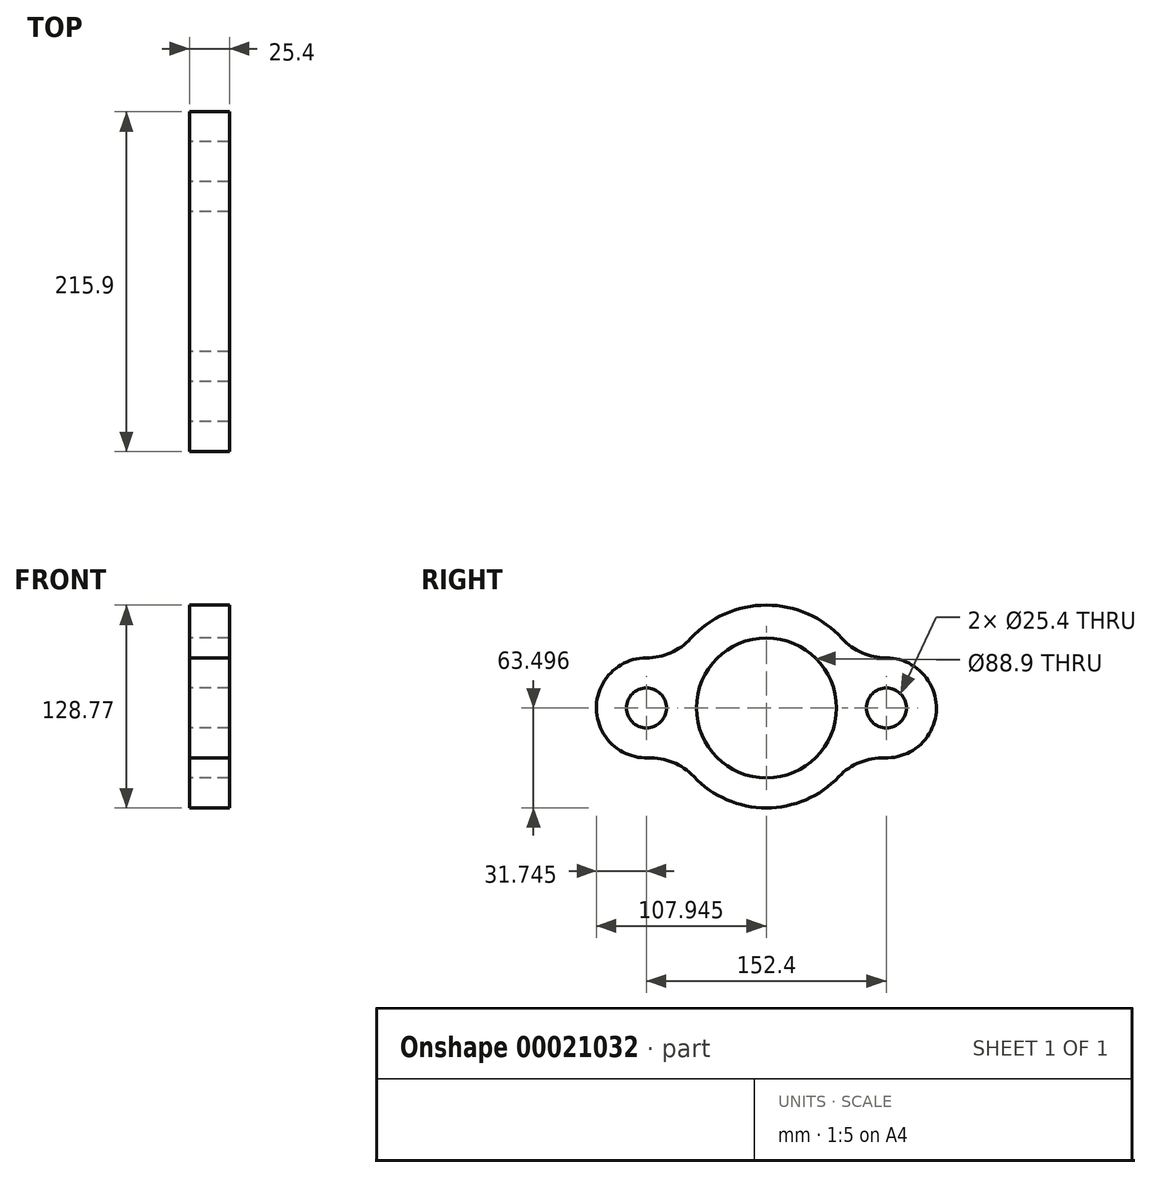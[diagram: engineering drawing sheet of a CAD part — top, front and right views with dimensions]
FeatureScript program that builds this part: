
annotation { "Feature Type Name" : "Feature", "Feature Type Description" : "" }
export const myFeature = defineFeature(function(context is Context, id is Id, definition is map)
    precondition{}
    {
        {
            var Q0;
            Q0=qCreatedBy(makeId("Right.planeOp"),FACE);
            var sketch = newSketch(context, id + "F0", { "sketchPlane" : qUnion([Q0])});
            skCircle(sketch, "E0", {"center": v(-83.32, 15.25) * mm, "radius": 12.7 * mm});
            skArc(sketch, "E1", {"start": v(-53.26, -28.38) * mm, "mid": v(-7.12, -48.25) * mm, "end": v(39.01, -28.38) * mm});
            skCircle(sketch, "E2", {"center": v(69.08, 15.25) * mm, "radius": 12.7 * mm});
            skArc(sketch, "E3", {"start": v(-83.32, 47) * mm, "mid": v(-115.07, 14.7) * mm, "end": v(-82.24, -16.49) * mm});
            skArc(sketch, "E4", {"start": v(68, -16.49) * mm, "mid": v(100.82, 14.7) * mm, "end": v(69.08, 47) * mm});
            skCircle(sketch, "E5", {"center": v(-7.12, 15.25) * mm, "radius": 44.45 * mm});
            skArc(sketch, "E6", {"start": v(-83.32, 47) * mm, "mid": v(-67.98, 50.22) * mm, "end": v(-55.24, 59.35) * mm});
            skArc(sketch, "E7", {"start": v(40.99, 59.35) * mm, "mid": v(53.73, 50.22) * mm, "end": v(69.08, 47) * mm});
            skArc(sketch, "E8.trimOffspring", {"start": v(40.99, 59.35) * mm, "mid": v(-7.12, 80.52) * mm, "end": v(-55.24, 59.35) * mm});
            skArc(sketch, "E9", {"start": v(-53.26, -28.38) * mm, "mid": v(-66.47, -19.32) * mm, "end": v(-82.24, -16.49) * mm});
            skArc(sketch, "E10", {"start": v(68, -16.49) * mm, "mid": v(52.22, -19.32) * mm, "end": v(39.01, -28.38) * mm});
            skSolve(sketch);
        }
        {
            var Q0;
            Q0 = qSketchRegion(id + "F0", true);
            extrude(context, id + "F1", {"entities" : qUnion([Q0]), "depth" : 25.4 * mm});
        }
        {
            var Q0;
            Q0 = qSketchRegion(id + "F0", true);
            extrude(context, id + "F2", {"entities" : qUnion([Q0]), "operationType" : NewBodyOperationType.ADD, "depth" : 25.4 * mm});
        }
        {
            var Q0;
            Q0 = qSketchRegion(id + "F0", true);
            extrude(context, id + "F3", {"entities" : qUnion([Q0]), "operationType" : NewBodyOperationType.ADD, "depth" : 25.4 * mm});
        }
    });
